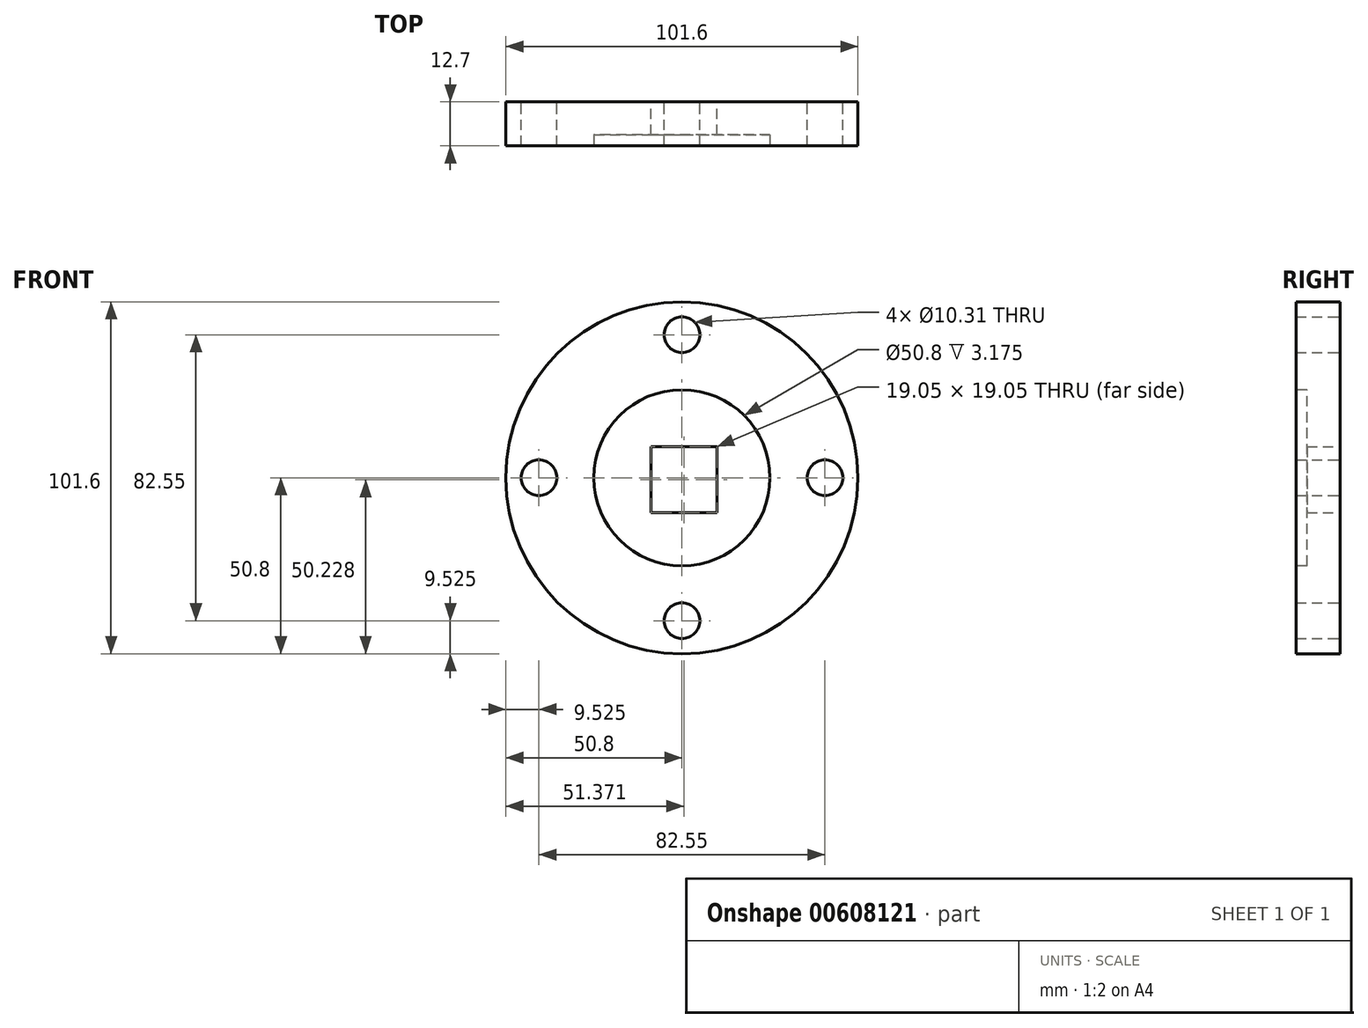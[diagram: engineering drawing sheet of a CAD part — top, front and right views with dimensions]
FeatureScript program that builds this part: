
annotation { "Feature Type Name" : "Feature", "Feature Type Description" : "" }
export const myFeature = defineFeature(function(context is Context, id is Id, definition is map)
    precondition{}
    {
        {
            var Q0;
            Q0=qCreatedBy(makeId("Front.planeOp"),FACE);
            var sketch = newSketch(context, id + "F0", { "sketchPlane" : qUnion([Q0])});
            skLineSegment(sketch, "E0.bottom", {"start": v(-8.95, 8.95) * mm, "end": v(10.1, 8.95) * mm});
            skLineSegment(sketch, "E0.top", {"start": v(-8.95, -10.1) * mm, "end": v(10.1, -10.1) * mm});
            skLineSegment(sketch, "E0.left", {"start": v(-8.95, 8.95) * mm, "end": v(-8.95, -10.1) * mm});
            skLineSegment(sketch, "E0.right", {"start": v(10.1, 8.95) * mm, "end": v(10.1, -10.1) * mm});
            skCircle(sketch, "E1", {"center": v(0, 0) * mm, "radius": 50.8 * mm});
            skCircle(sketch, "E2", {"center": v(0, 41.28) * mm, "radius": 5.16 * mm});
            skCircle(sketch, "E3", {"center": v(-41.28, 0) * mm, "radius": 5.16 * mm});
            skCircle(sketch, "E4", {"center": v(41.28, 0) * mm, "radius": 5.16 * mm});
            skCircle(sketch, "E5", {"center": v(0, -41.28) * mm, "radius": 5.16 * mm});
            skSolve(sketch);
        }
        {
            var Q0;
            Q0=makeQuery(id+"F0.imprint","IMPRINT",FACE,{"disambiguationData":[TD([[makeQuery(id+"F0.imprint","IMPRINT",EDGE,{"derivedFrom":sQuery(id+"F0.wireOp",EDGE,"E0.bottom")}),1.0]])]});
            extrude(context, id + "F1", {"entities" : qUnion([Q0]), "depth" : 12.7 * mm, "offsetDistance" : 25.4 * mm});
        }
        {
            var Q0;
            Q0=makeQuery(id+"F1.opExtrude","CAP_FACE",FACE,{"disambiguationData":[OSD([sQuery(id+"F0.wireOp",EDGE,"E0.bottom"),sQuery(id+"F0.wireOp",EDGE,"E0.top"),sQuery(id+"F0.wireOp",EDGE,"E0.left"),sQuery(id+"F0.wireOp",EDGE,"E0.right"),sQuery(id+"F0.wireOp",EDGE,"E1"),sQuery(id+"F0.wireOp",EDGE,"E2"),sQuery(id+"F0.wireOp",EDGE,"E3"),sQuery(id+"F0.wireOp",EDGE,"E4"),sQuery(id+"F0.wireOp",EDGE,"E5")])],"isStart":false});
            var sketch = newSketch(context, id + "F2", { "sketchPlane" : qUnion([Q0])});
            skCircle(sketch, "E6", {"center": v(0, 0) * mm, "radius": 25.4 * mm});
            skSolve(sketch);
        }
        {
            var Q0;
            Q0=makeQuery(id+"F2.imprint","IMPRINT",FACE,{"disambiguationData":[TD([[makeQuery(id+"F2.imprint","IMPRINT",EDGE,{"derivedFrom":sQuery(id+"F2.wireOp",EDGE,"E6")}),1.0]])]});
            extrude(context, id + "F3", {"entities" : qUnion([Q0]), "operationType" : NewBodyOperationType.REMOVE, "oppositeDirection" : true, "depth" : 3.17 * mm, "offsetDistance" : 25.4 * mm});
        }
    });
